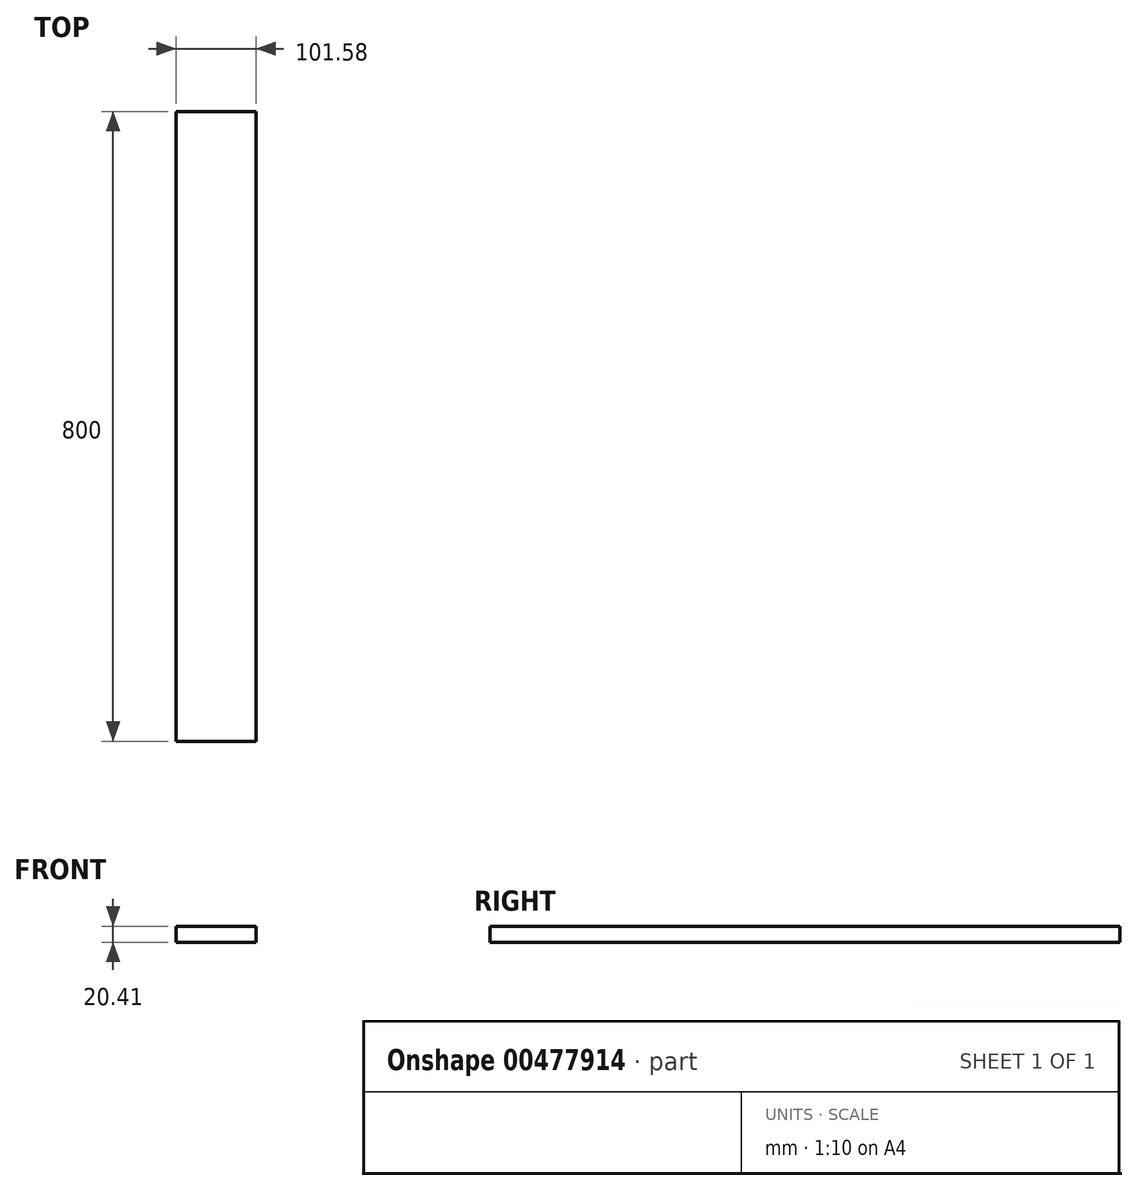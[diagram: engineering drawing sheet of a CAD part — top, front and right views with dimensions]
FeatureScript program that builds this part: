
annotation { "Feature Type Name" : "Feature", "Feature Type Description" : "" }
export const myFeature = defineFeature(function(context is Context, id is Id, definition is map)
    precondition{}
    {
        {
            var Q0;
            Q0=qCreatedBy(makeId("Front.planeOp"),FACE);
            var sketch = newSketch(context, id + "F0", { "sketchPlane" : qUnion([Q0])});
            skLineSegment(sketch, "E0.bottom", {"start": v(0, 0) * mm, "end": v(101.58, 0) * mm});
            skLineSegment(sketch, "E0.top", {"start": v(0, 20.41) * mm, "end": v(101.58, 20.41) * mm});
            skLineSegment(sketch, "E0.left", {"start": v(0, 0) * mm, "end": v(0, 20.41) * mm});
            skLineSegment(sketch, "E0.right", {"start": v(101.58, 0) * mm, "end": v(101.58, 20.41) * mm});
            skSolve(sketch);
        }
        {
            var Q0;
            Q0 = qSketchRegion(id + "F0", true);
            extrude(context, id + "F1", {"entities" : qUnion([Q0]), "depth" : 800 * mm});
        }
    });
